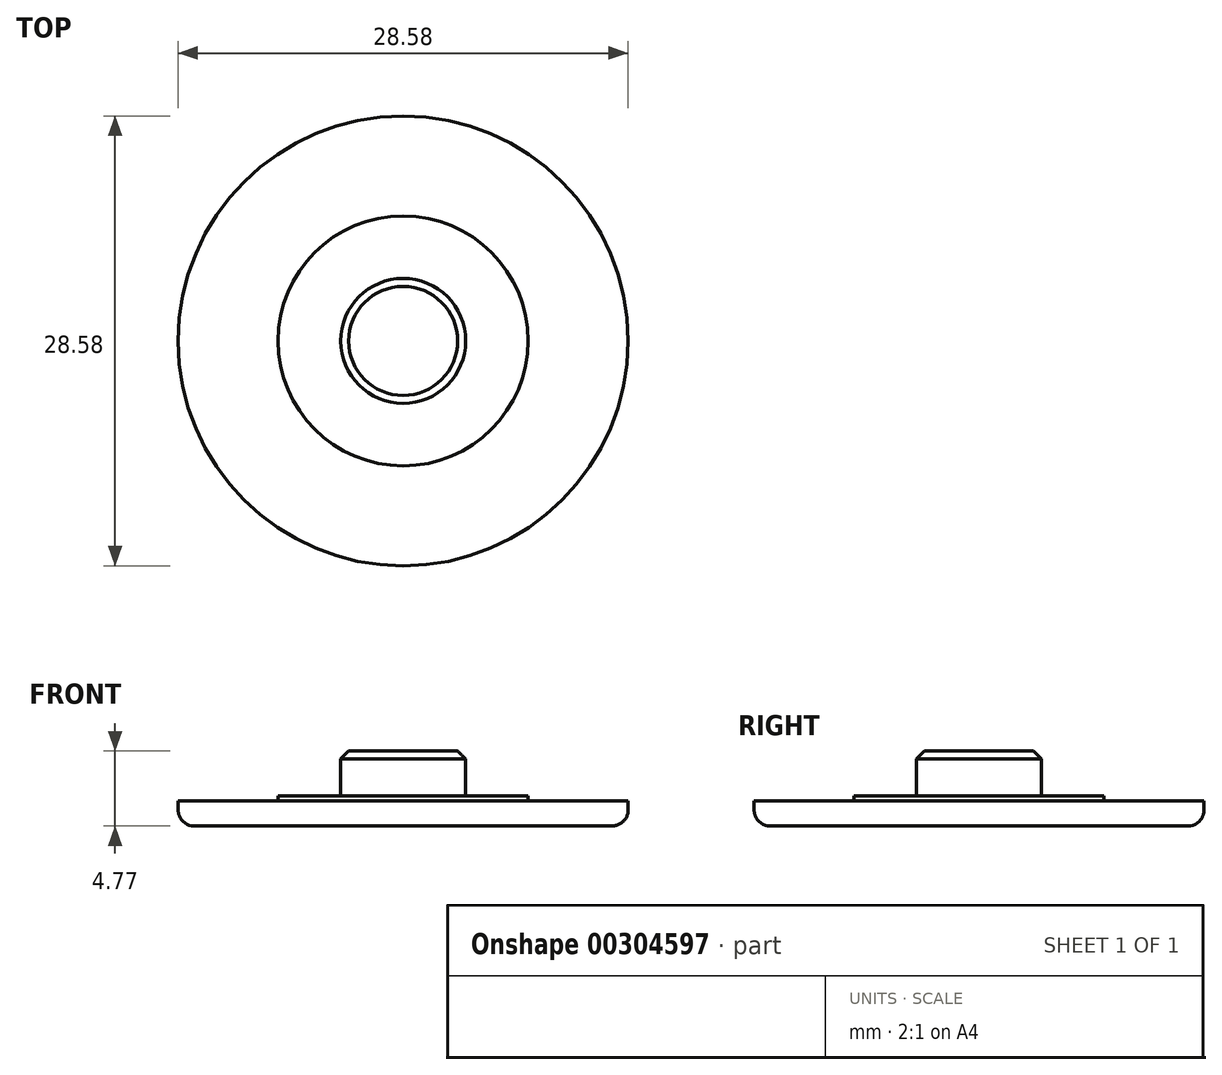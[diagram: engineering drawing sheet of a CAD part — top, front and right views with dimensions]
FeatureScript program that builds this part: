
annotation { "Feature Type Name" : "Feature", "Feature Type Description" : "" }
export const myFeature = defineFeature(function(context is Context, id is Id, definition is map)
    precondition{}
    {
        {
            var Q0;
            Q0=qCreatedBy(makeId("Top.planeOp"),FACE);
            var sketch = newSketch(context, id + "F0", { "sketchPlane" : qUnion([Q0])});
            skCircle(sketch, "E0", {"center": v(0, 0) * mm, "radius": 14.29 * mm});
            skCircle(sketch, "E1", {"center": v(0, 0) * mm, "radius": 3.97 * mm});
            skCircle(sketch, "E2", {"center": v(0, 0) * mm, "radius": 7.94 * mm});
            skSolve(sketch);
        }
        {
            var Q0;
            Q0=makeQuery(id+"F0.imprint","IMPRINT",FACE,{"disambiguationData":[TD([[makeQuery(id+"F0.imprint","IMPRINT",EDGE,{"derivedFrom":sQuery(id+"F0.wireOp",EDGE,"E0")}),1.0]])]});
            var Q1;
            Q1=makeQuery(id+"F0.imprint","IMPRINT",FACE,{"disambiguationData":[TD([[makeQuery(id+"F0.imprint","IMPRINT",EDGE,{"derivedFrom":sQuery(id+"F0.wireOp",EDGE,"E1")}),1.0]])]});
            var Q2;
            Q2=makeQuery(id+"F0.imprint","IMPRINT",FACE,{"disambiguationData":[TD([[makeQuery(id+"F0.imprint","IMPRINT",EDGE,{"derivedFrom":sQuery(id+"F0.wireOp",EDGE,"E1")}),-1.0]])]});
            extrude(context, id + "F1", {"entities" : qUnion([Q0, Q1, Q2]), "oppositeDirection" : true, "depth" : 1.59 * mm});
        }
        {
            var Q0;
            Q0=makeQuery(id+"F0.imprint","IMPRINT",FACE,{"disambiguationData":[TD([[makeQuery(id+"F0.imprint","IMPRINT",EDGE,{"derivedFrom":sQuery(id+"F0.wireOp",EDGE,"E1")}),1.0]])]});
            extrude(context, id + "F2", {"entities" : qUnion([Q0]), "operationType" : NewBodyOperationType.ADD, "depth" : 3.17 * mm});
        }
        {
            var Q0;
            Q0=makeQuery(id+"F1.opExtrude","CAP_EDGE",EDGE,{"disambiguationData":[OSD([sQuery(id+"F0.wireOp",EDGE,"E0")])],"isStart":false});
            fillet(context, id + "F3", {"entities" : qUnion([Q0]), "radius" : 1.02 * mm, "tangentPropagation" : true, "allowEdgeOverflow" : false});
        }
        {
            var Q0;
            Q0=makeQuery(id+"F0.imprint","IMPRINT",FACE,{"disambiguationData":[TD([[makeQuery(id+"F0.imprint","IMPRINT",EDGE,{"derivedFrom":sQuery(id+"F0.wireOp",EDGE,"E1")}),-1.0]])]});
            extrude(context, id + "F4", {"entities" : qUnion([Q0]), "operationType" : NewBodyOperationType.ADD, "depth" : 0.32 * mm});
        }
        {
            var Q0;
            Q0=makeQuery(id+"F2.opExtrude","CAP_EDGE",EDGE,{"disambiguationData":[OSD([sQuery(id+"F0.wireOp",EDGE,"E1")])],"isStart":false});
            chamfer(context, id + "F5", {"entities" : qUnion([Q0]), "width" : 0.5 * mm, "tangentPropagation" : true});
        }
    });
